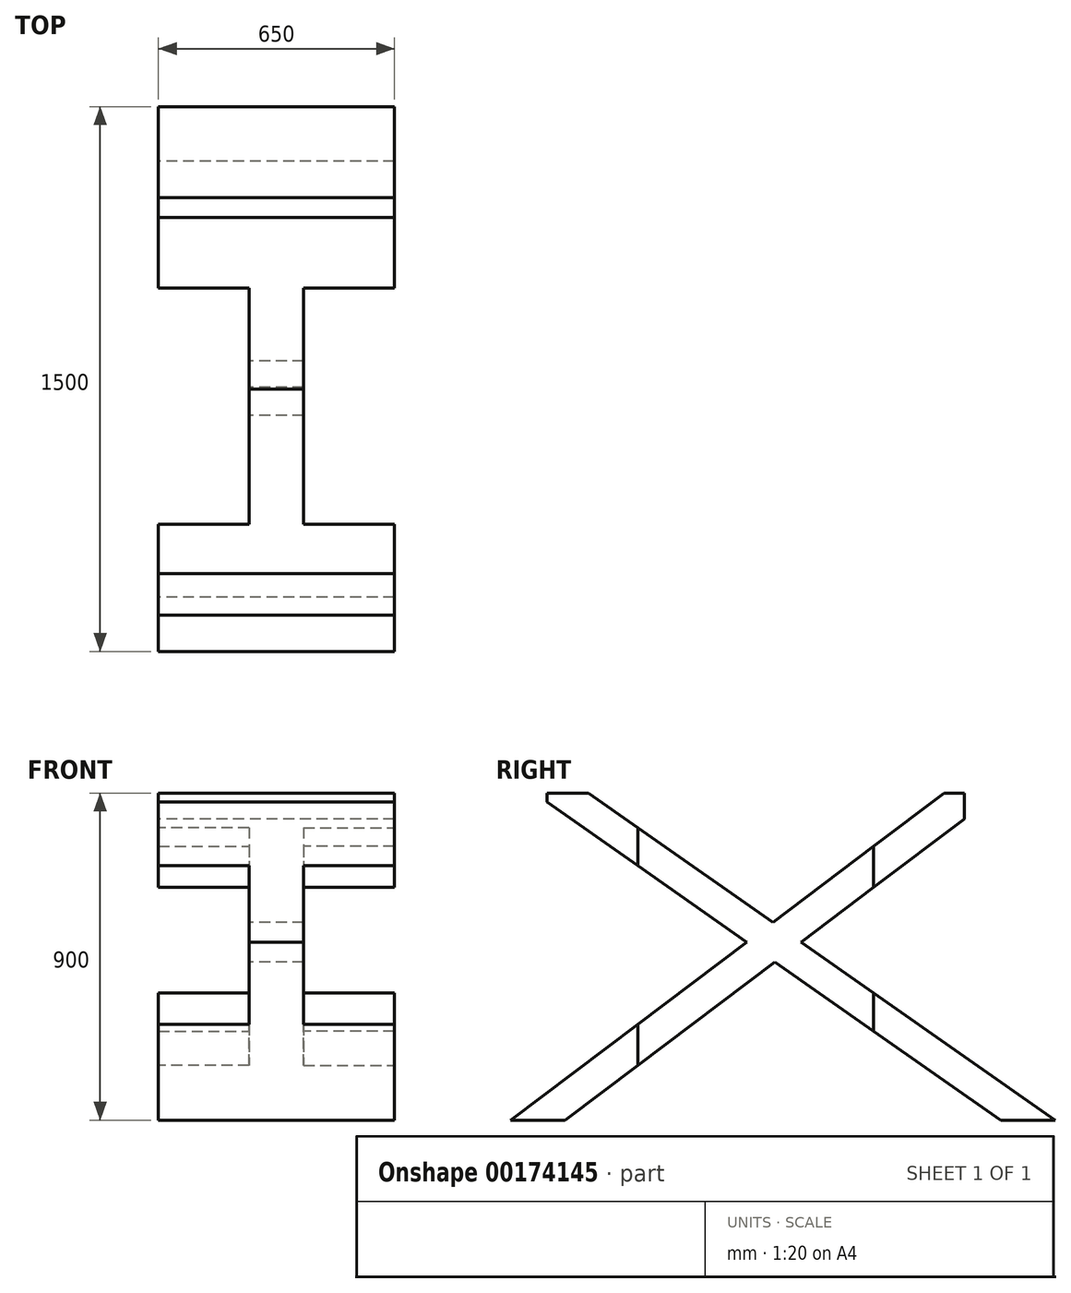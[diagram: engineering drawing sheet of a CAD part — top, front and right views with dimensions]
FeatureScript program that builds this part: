
annotation { "Feature Type Name" : "Feature", "Feature Type Description" : "" }
export const myFeature = defineFeature(function(context is Context, id is Id, definition is map)
    precondition{}
    {
        {
            var Q0;
            Q0=qCreatedBy(makeId("Right.planeOp"),FACE);
            var sketch = newSketch(context, id + "F0", { "sketchPlane" : qUnion([Q0])});
            skLineSegment(sketch, "E0", {"start": v(0, 0) * mm, "end": v(150, 0) * mm});
            skLineSegment(sketch, "E1", {"start": v(150, 0) * mm, "end": v(1250, 828.9) * mm});
            skLineSegment(sketch, "E2", {"start": v(1250, 828.9) * mm, "end": v(1250, 900) * mm});
            skLineSegment(sketch, "E3", {"start": v(1250, 900) * mm, "end": v(1194.34, 900) * mm});
            skLineSegment(sketch, "E4", {"start": v(1194.34, 900) * mm, "end": v(0, 0) * mm});
            skLineSegment(sketch, "E5", {"start": v(1350, 0) * mm, "end": v(100, 875.26) * mm});
            skLineSegment(sketch, "E6", {"start": v(100, 875.26) * mm, "end": v(100, 900) * mm});
            skLineSegment(sketch, "E7", {"start": v(100, 900) * mm, "end": v(214.67, 900) * mm});
            skLineSegment(sketch, "E8", {"start": v(214.67, 900) * mm, "end": v(1500, 0) * mm});
            skLineSegment(sketch, "E9", {"start": v(1500, 0) * mm, "end": v(1350, 0) * mm});
            skSolve(sketch);
        }
        {
            var Q0;
            {var subQ1=sQuery(id+"F0.wireOp",EDGE,"E6");Q0=makeQuery(id+"F0.imprint","IMPRINT",FACE,{"disambiguationData":[TD([[makeQuery(id+"F0.imprint","IMPRINT",EDGE,{"derivedFrom":subQ1}),-1.0]])]});}
            var Q1;
            {var subQ0=sQuery(id+"F0.wireOp",EDGE,"E0");Q1=makeQuery(id+"F0.imprint","IMPRINT",FACE,{"disambiguationData":[TD([[makeQuery(id+"F0.imprint","IMPRINT",EDGE,{"derivedFrom":subQ0}),1.0]])]});}
            var Q2;
            {var subQ0=sQuery(id+"F0.wireOp",EDGE,"E5");var subQ1=sQuery(id+"F0.wireOp",EDGE,"E1");var subQ2=makeQuery(id+"F0.imprint","INTERSECT",VERTEX,{"derivedFrom":[subQ1,subQ0]});Q2=makeQuery(id+"F0.imprint","IMPRINT",FACE,{"disambiguationData":[TD([[makeQuery(id+"F0.imprint","IMPRINT",EDGE,{"disambiguationData":[TD([[subQ2,-1.0]])],"derivedFrom":subQ1}),1.0]])]});}
            var Q3;
            {var subQ4=sQuery(id+"F0.wireOp",EDGE,"E2");Q3=makeQuery(id+"F0.imprint","IMPRINT",FACE,{"disambiguationData":[TD([[makeQuery(id+"F0.imprint","IMPRINT",EDGE,{"derivedFrom":subQ4}),1.0]])]});}
            var Q4;
            {var subQ5=sQuery(id+"F0.wireOp",EDGE,"E9");Q4=makeQuery(id+"F0.imprint","IMPRINT",FACE,{"disambiguationData":[TD([[makeQuery(id+"F0.imprint","IMPRINT",EDGE,{"derivedFrom":subQ5}),-1.0]])]});}
            extrude(context, id + "F1", {"entities" : qUnion([Q0, Q1, Q2, Q3, Q4]), "endBound" : BoundingType.SYMMETRIC, "depth" : 650 * mm});
        }
        {
            var Q0;
            Q0=qCreatedBy(makeId("Top.planeOp"),FACE);
            var sketch = newSketch(context, id + "F2", { "sketchPlane" : qUnion([Q0])});
            skLineSegment(sketch, "E10.bottom", {"start": v(-325, 1000) * mm, "end": v(-75, 1000) * mm});
            skLineSegment(sketch, "E10.top", {"start": v(-325, 350) * mm, "end": v(-75, 350) * mm});
            skLineSegment(sketch, "E10.left", {"start": v(-325, 1000) * mm, "end": v(-325, 350) * mm});
            skLineSegment(sketch, "E10.right", {"start": v(-75, 1000) * mm, "end": v(-75, 350) * mm});
            skLineSegment(sketch, "E11.MirrorCS", {"start": v(325, 1000) * mm, "end": v(75, 1000) * mm});
            skLineSegment(sketch, "E12.MirrorCS", {"start": v(325, 1000) * mm, "end": v(325, 350) * mm});
            skLineSegment(sketch, "E13.MirrorCS", {"start": v(75, 1000) * mm, "end": v(75, 350) * mm});
            skLineSegment(sketch, "E14.MirrorCS", {"start": v(325, 350) * mm, "end": v(75, 350) * mm});
            skSolve(sketch);
        }
        {
            var Q0;
            Q0=makeQuery(id+"F2.imprint","IMPRINT",FACE,{"disambiguationData":[TD([[makeQuery(id+"F2.imprint","IMPRINT",EDGE,{"derivedFrom":sQuery(id+"F2.wireOp",EDGE,"E11.MirrorCS")}),1.0]])]});
            var Q1;
            Q1=makeQuery(id+"F2.imprint","IMPRINT",FACE,{"disambiguationData":[TD([[makeQuery(id+"F2.imprint","IMPRINT",EDGE,{"derivedFrom":sQuery(id+"F2.wireOp",EDGE,"E10.bottom")}),-1.0]])]});
            var Q2;
            Q2=makeQuery(id+"F1.opExtrude","SWEPT_FACE",FACE,{"disambiguationData":[OSD([sQuery(id+"F0.wireOp",EDGE,"E7")])]});
            extrude(context, id + "F3", {"entities" : qUnion([Q0, Q1]), "operationType" : NewBodyOperationType.REMOVE, "endBound" : BoundingType.UP_TO_SURFACE, "endBoundEntityFace" : qUnion([Q2]), "depth" : 25 * mm});
        }
    });
